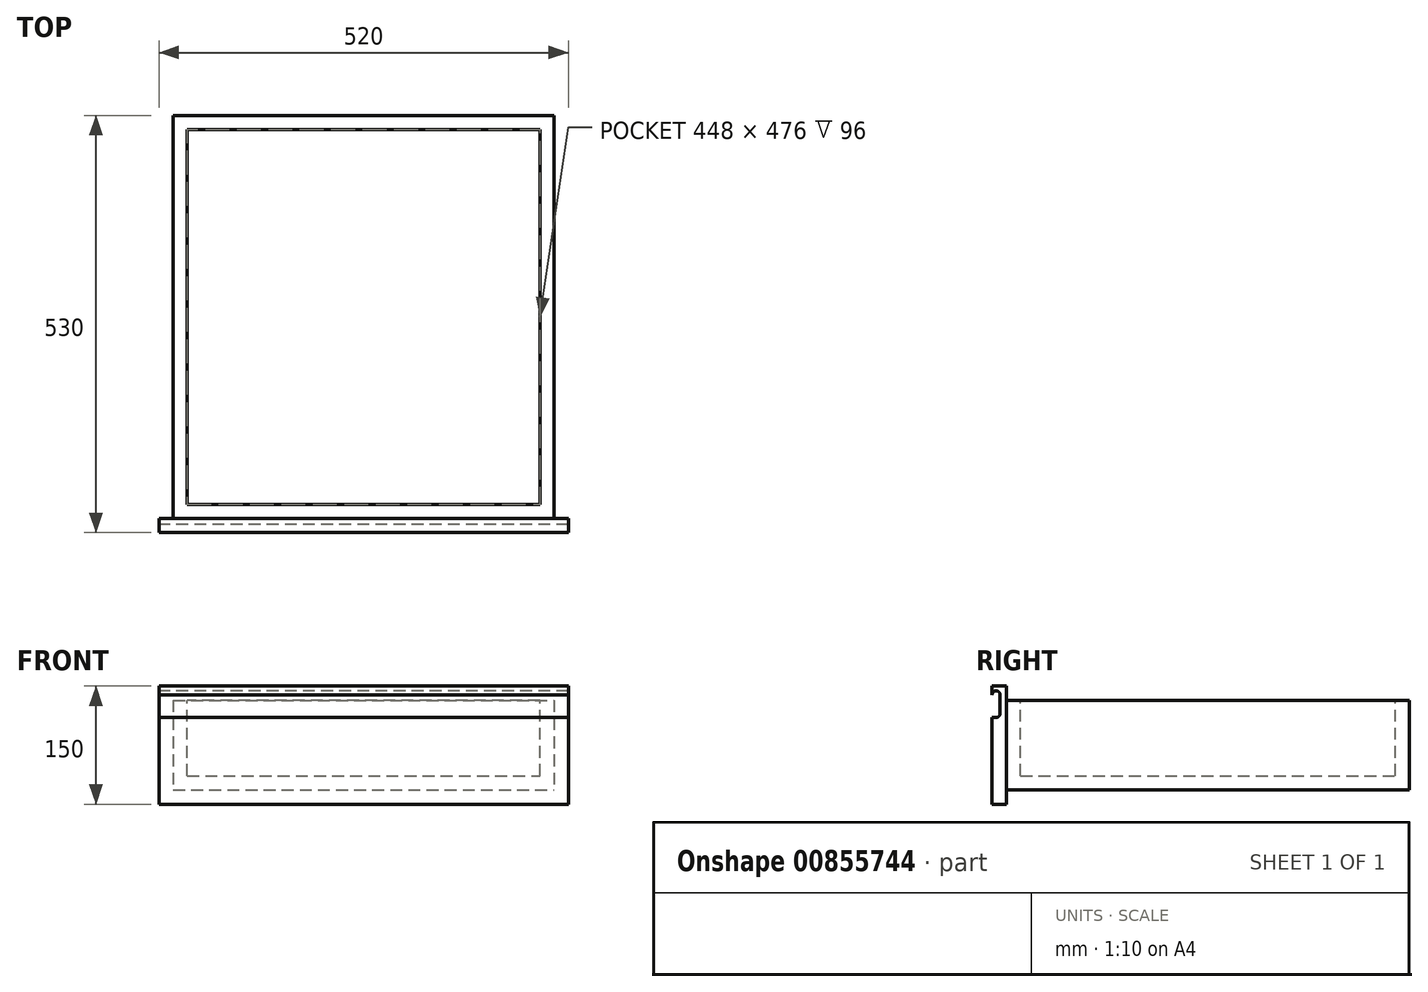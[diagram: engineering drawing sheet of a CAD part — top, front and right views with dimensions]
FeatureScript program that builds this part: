
annotation { "Feature Type Name" : "Feature", "Feature Type Description" : "" }
export const myFeature = defineFeature(function(context is Context, id is Id, definition is map)
    precondition{}
    {
        {
            var Q0;
            Q0=qCreatedBy(makeId("Front.planeOp"),FACE);
            var sketch = newSketch(context, id + "F0", { "sketchPlane" : qUnion([Q0])});
            skLineSegment(sketch, "E0", {"start": v(0, 150) * mm, "end": v(520, 150) * mm});
            skLineSegment(sketch, "E1", {"start": v(0, 150) * mm, "end": v(0, 0) * mm});
            skLineSegment(sketch, "E2", {"start": v(520, 150) * mm, "end": v(520, 0) * mm});
            skLineSegment(sketch, "E3", {"start": v(0, 0) * mm, "end": v(520, 0) * mm});
            skLineSegment(sketch, "E4.0", {"start": v(18, 18) * mm, "end": v(502, 18) * mm});
            skLineSegment(sketch, "E4.1", {"start": v(18, 132) * mm, "end": v(18, 18) * mm});
            skLineSegment(sketch, "E4.2", {"start": v(18, 132) * mm, "end": v(502, 132) * mm});
            skLineSegment(sketch, "E4.3", {"start": v(502, 132) * mm, "end": v(502, 18) * mm});
            skSolve(sketch);
        }
        {
            var Q0;
            Q0 = qSketchRegion(id + "F0", true);
            extrude(context, id + "F1", {"entities" : qUnion([Q0]), "oppositeDirection" : true, "depth" : 18 * mm, "offsetDistance" : 25 * mm});
        }
        {
            var Q0;
            Q0=makeQuery(id+"F0.imprint","IMPRINT",FACE,{"disambiguationData":[TD([[makeQuery(id+"F0.imprint","IMPRINT",EDGE,{"derivedFrom":sQuery(id+"F0.wireOp",EDGE,"E4.0")}),1.0]])]});
            extrude(context, id + "F2", {"entities" : qUnion([Q0]), "operationType" : NewBodyOperationType.ADD, "oppositeDirection" : true, "depth" : 530 * mm, "offsetDistance" : 25 * mm});
        }
        {
            var Q0;
            Q0=makeQuery(id+"F2.opExtrude","SWEPT_FACE",FACE,{"disambiguationData":[OSD([sQuery(id+"F0.wireOp",EDGE,"E4.2")])]});
            var sketch = newSketch(context, id + "F3", { "sketchPlane" : qUnion([Q0])});
            skLineSegment(sketch, "E5", {"start": v(18, 18) * mm, "end": v(36, 18) * mm});
            skLineSegment(sketch, "E6", {"start": v(36, 36) * mm, "end": v(36, 512) * mm});
            skLineSegment(sketch, "E7", {"start": v(484, 512) * mm, "end": v(36, 512) * mm});
            skLineSegment(sketch, "E8", {"start": v(484, 36) * mm, "end": v(484, 512) * mm});
            skLineSegment(sketch, "E9", {"start": v(36, 36) * mm, "end": v(484, 36) * mm});
            skSolve(sketch);
        }
        {
            var Q0;
            Q0=makeQuery(id+"F3.imprint","IMPRINT",FACE,{"disambiguationData":[TD([[makeQuery(id+"F3.imprint","IMPRINT",EDGE,{"derivedFrom":sQuery(id+"F3.wireOp",EDGE,"E6")}),-1.0]])]});
            extrude(context, id + "F4", {"entities" : qUnion([Q0]), "operationType" : NewBodyOperationType.REMOVE, "oppositeDirection" : true, "depth" : 96 * mm, "offsetDistance" : 25 * mm});
        }
        {
            var Q0;
            Q0=makeQuery(id+"F1.opExtrude","SWEPT_FACE",FACE,{"disambiguationData":[OSD([sQuery(id+"F0.wireOp",EDGE,"E1")])]});
            var sketch = newSketch(context, id + "F5", { "sketchPlane" : qUnion([Q0])});
            skLineSegment(sketch, "E10", {"start": v(0, 110) * mm, "end": v(-5, 110) * mm});
            skLineSegment(sketch, "E11", {"start": v(-10, 115) * mm, "end": v(-10, 139) * mm});
            skArc(sketch, "E12", {"start": v(0, 139) * mm, "mid": v(-5, 144) * mm, "end": v(-10, 139) * mm});
            skPoint(sketch, "E13.visualSharp", {"position": v(-10, 110) * mm});
            skArc(sketch, "E13.filletArc", {"start": v(-10, 115) * mm, "mid": v(-8.54, 111.46) * mm, "end": v(-5, 110) * mm});
            skSolve(sketch);
        }
        {
            var Q0;
            {var subQ1=sQuery(id+"F5.wireOp",EDGE,"E10");Q0=makeQuery(id+"F5.imprint","IMPRINT",FACE,{"disambiguationData":[TD([[makeQuery(id+"F5.imprint","IMPRINT",EDGE,{"derivedFrom":subQ1}),-1.0]])]});}
            extrude(context, id + "F6", {"entities" : qUnion([Q0]), "operationType" : NewBodyOperationType.REMOVE, "oppositeDirection" : true, "depth" : 539 * mm, "offsetDistance" : 25 * mm});
        }
    });
